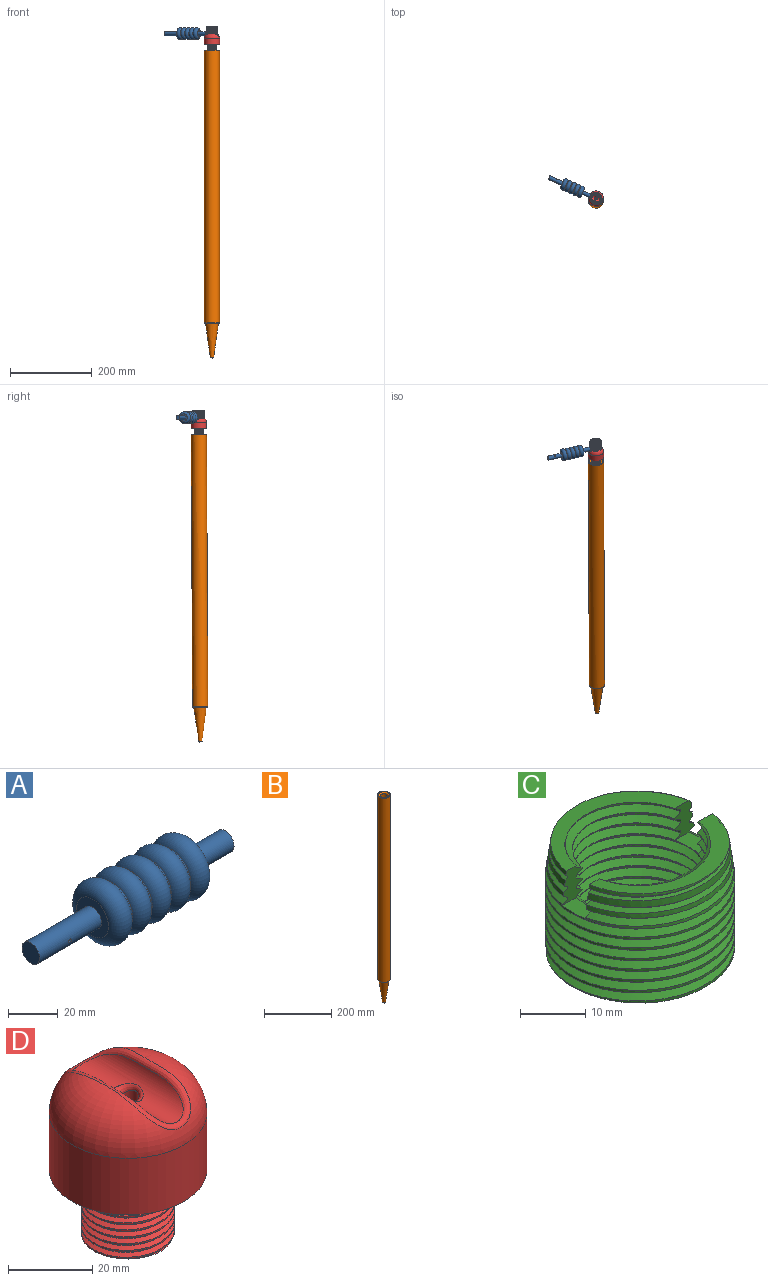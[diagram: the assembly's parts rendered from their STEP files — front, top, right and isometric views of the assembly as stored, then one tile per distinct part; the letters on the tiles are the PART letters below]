
ASSEMBLY  parts=4 mates=3
PART A: 18 faces, bbox 110x31.4x31.4 mm
  f0: cylinder r=5mm len=35mm, axis (-1,0,0), area 1081.4mm2, adj f3,f4,f15,f17
  f1: torus R=11.4mm, axis (-1,0,0), area 80.2mm2, adj f2,f14
  f2: torus R=9mm, axis (-1,0,0), area 1213.5mm2, adj f1,f3
  f3: plane 18x18mm, normal (-1,0,0), area 175.9mm2, adj f0,f2
  f4: plane 10x10mm, normal (-1,0,0), area 78.5mm2, adj f0
  f5: plane 10x10mm, normal (1,0,0), area 78.5mm2, adj f6
  f6: cylinder r=5mm len=20mm, axis (-1,0,0), area 628.3mm2, adj f5,f7
  f7: plane 18x18mm, normal (1,0,0), area 175.9mm2, adj f6,f8
  f8: torus R=9mm, axis (-1,0,0), area 1213.5mm2, adj f7,f9
  f9: torus R=11.4mm, axis (-1,0,0), area 80.2mm2, adj f8,f10
  f10: torus R=9mm, axis (-1,0,0), area 1069.8mm2, adj f9,f11
  f11: torus R=11.4mm, axis (-1,0,0), area 80.2mm2, adj f10,f12
  f12: torus R=9mm, axis (-1,0,0), area 1069.8mm2, adj f11,f13
  f13: torus R=11.4mm, axis (-1,0,0), area 80.2mm2, adj f12,f14
  f14: torus R=9mm, axis (-1,0,0), area 1069.8mm2, adj f1,f13
  f15: cylinder r=2.25mm len=5mm, axis (0,-1,0), area 67mm2, adj f0,f16
  f16: plane 4.5x4.5mm, normal (0,1,0), area 14.1mm2, adj f15,f17
  f17: cylinder r=0.75mm len=5mm, axis (0,1,0), area 23.4mm2, adj f0,f16
PART B: 10 faces, bbox 40.6x40.6x755 mm
  f0: plane 35.5x35.5mm, normal (0,0,-1), area 210.5mm2, adj f1,f9
  f1: cone r=15.75mm half-angle=7.9deg, axis (0,0,1), area 5279mm2, adj f0,f2
  f2: torus R=2.26mm, axis (0,0,1), area 62.4mm2, adj f1,f3
  f3: plane 4.52x4.52mm, normal (0,0,-1), area 16mm2, adj f2
  f4: plane 22x22mm, normal (0,0,1), area 380.1mm2, adj f5
  f5: cylinder r=11mm len=43mm, axis (0,0,1), area 2971.9mm2, adj f4,f6
  f6: torus R=16mm, axis (0,0,1), area 632.5mm2, adj f5,f7
  f7: plane 37.5x37.5mm, normal (0,0,1), area 300.2mm2, adj f6,f8
  f8: cylinder r=18.75mm len=669mm, axis (0,0,1), area 78814.7mm2, adj f7,f9
  f9: torus R=17.75mm, axis (0,0,1), area 181.5mm2, adj f0,f8
PART C: 67 faces, bbox 29.9x34.4x22.6 mm
  f0: bspline ~29.17x16.84mm, area 16.2mm2, adj f2,f3,f8,f29,f66
  f1: bspline ~21.88x16.84mm, area 4mm2, adj f19,f20,f34,f61
  f2: plane 6.02x4.22mm, normal (0,1,0), area 17.3mm2, adj f0,f5,f8,f9,f10,f14,f15,f16
  f3: plane 6.02x4.31mm, normal (0,1,0), area 17.2mm2, adj f0,f8,f9,f10,f14,f15,f16,f22
  f4: plane 6.02x4.31mm, normal (0,-1,0), area 17.1mm2, adj f7,f11,f12,f13,f17,f18,f19,f21
  f5: bspline ~33.69x29.17mm, area 858.4mm2, adj f2,f6,f28,f35,f36,f62
  f6: cylinder r=14.59mm len=29.17mm, axis (0,0,-1), area 442.2mm2, adj f5,f7,f36,f37,f62,f65
  f7: bspline ~33.69x29.17mm, area 882.5mm2, adj f4,f6,f35,f36,f65
  f8: plane 26.86x11.33mm, normal (0,0,1), area 85.6mm2, adj f0,f2,f3,f57,f58,f66
  f9: bspline ~29.17x16.84mm, area 28.7mm2, adj f2,f3,f30,f64
  f10: bspline ~29.17x16.84mm, area 40.6mm2, adj f2,f3,f31,f63
  f11: bspline ~29.17x16.84mm, area 22.9mm2, adj f4,f20,f33,f61
  f12: bspline ~29.17x16.84mm, area 34.6mm2, adj f4,f20,f32,f60
  f13: bspline ~29.17x16.84mm, area 46.6mm2, adj f4,f20,f35,f59
  f14: bspline ~29.17x16.84mm, area 21.3mm2, adj f2,f3,f29,f64
  f15: bspline ~29.17x16.84mm, area 35.1mm2, adj f2,f3,f30,f63
  f16: bspline ~29.17x16.84mm, area 49.3mm2, adj f2,f3,f31,f62
  f17: bspline ~29.17x16.84mm, area 28.2mm2, adj f4,f20,f33,f60
  f18: bspline ~29.17x16.84mm, area 42.2mm2, adj f4,f20,f32,f59
  f19: plane 27.4x11.98mm, normal (0,0,1), area 88.6mm2, adj f1,f4,f20,f27,f34,f49,f50,f61
  f20: plane 6.02x4.21mm, normal (0,-1,0), area 17.2mm2, adj f1,f11,f12,f13,f17,f18,f19,f21
  f21: cylinder r=10.39mm len=20.77mm, axis (0,0,-1), area 71.1mm2, adj f4,f20,f28,f36,f39,f41,f45
  f22: cylinder r=10.39mm len=20.16mm, axis (0,0,-1), area 3.6mm2, adj f2,f3,f40,f54
  f23: cylinder r=10.39mm len=20.16mm, axis (0,0,-1), area 3.6mm2, adj f4,f20,f42,f46
  f24: cylinder r=10.39mm len=20.16mm, axis (0,0,-1), area 3.6mm2, adj f2,f3,f51,f55
  f25: cylinder r=10.39mm len=20.16mm, axis (0,0,-1), area 3.6mm2, adj f4,f20,f43,f48
  f26: cylinder r=10.39mm len=20.16mm, axis (0,0,-1), area 3.6mm2, adj f2,f3,f52,f58
  f27: cylinder r=10.39mm len=1.66mm, axis (0,0,-1), area 0mm2, adj f19,f20,f50
  f28: plane 5.04x3.36mm, normal (0,0,1), area 15.1mm2, adj f2,f5,f20,f21,f35,f41
  f29: cylinder r=13.39mm len=26.3mm, axis (0,0,-1), area 6.1mm2, adj f0,f2,f3,f14
  f30: cylinder r=13.39mm len=26.3mm, axis (0,0,-1), area 6.1mm2, adj f2,f3,f9,f15
  f31: cylinder r=13.39mm len=26.3mm, axis (0,0,-1), area 6.1mm2, adj f2,f3,f10,f16
  f32: cylinder r=13.39mm len=26.3mm, axis (0,0,-1), area 6.1mm2, adj f4,f12,f18,f20
  f33: cylinder r=13.39mm len=26.3mm, axis (0,0,-1), area 6.1mm2, adj f4,f11,f17,f20
  f34: cylinder r=13.39mm len=4.11mm, axis (0,0,-1), area 0.2mm2, adj f1,f19,f20
  f35: cylinder r=13.39mm len=26.77mm, axis (0,0,-1), area 20.3mm2, adj f4,f5,f7,f13,f20,f28,f36
  f36: plane 29.01x28.75mm, normal (0,0,-1), area 235mm2, adj f5,f6,f7,f21,f35,f38,f39,f41
  f37: plane 5x3.24mm, normal (0,0,1), area 14.9mm2, adj f3,f4,f6,f38
  f38: cylinder r=11.62mm len=23.23mm, axis (0,0,1), area 329.8mm2, adj f2,f3,f4,f36,f37,f39,f40,f41
  f39: bspline ~26.83x23.23mm, area 707.9mm2, adj f4,f21,f36,f38
  f40: bspline ~23.23x13.41mm, area 41.9mm2, adj f2,f3,f22,f38
  f41: bspline ~26.83x23.23mm, area 701.3mm2, adj f2,f21,f28,f36,f38
  f42: bspline ~23.23x13.41mm, area 41.9mm2, adj f4,f20,f23,f44
  f43: bspline ~23.23x13.41mm, area 41.9mm2, adj f4,f20,f25,f44
  f44: cylinder r=11.62mm len=22.69mm, axis (0,0,1), area 14.2mm2, adj f4,f20,f42,f43
  f45: bspline ~23.23x13.41mm, area 41.9mm2, adj f4,f20,f21,f47
  f46: bspline ~23.23x13.41mm, area 41.9mm2, adj f4,f20,f23,f47
  f47: cylinder r=11.62mm len=22.69mm, axis (0,0,1), area 14.2mm2, adj f4,f20,f45,f46
  f48: bspline ~23.23x13.41mm, area 41.9mm2, adj f4,f20,f25,f49
  f49: cylinder r=11.62mm len=22.69mm, axis (0,0,1), area 14mm2, adj f4,f19,f20,f48,f50
  f50: bspline ~23.23x13.41mm, area 20.6mm2, adj f19,f20,f27,f49
  f51: bspline ~23.23x13.41mm, area 41.9mm2, adj f2,f3,f24,f53
  f52: bspline ~23.23x13.41mm, area 41.9mm2, adj f2,f3,f26,f53
  f53: cylinder r=11.62mm len=22.69mm, axis (0,0,1), area 14.2mm2, adj f2,f3,f51,f52
  f54: bspline ~23.23x13.41mm, area 41.9mm2, adj f2,f3,f22,f56
  f55: bspline ~23.23x13.41mm, area 41.9mm2, adj f2,f3,f24,f56
  f56: cylinder r=11.62mm len=22.69mm, axis (0,0,1), area 14.2mm2, adj f2,f3,f54,f55
  f57: cylinder r=11.62mm len=6.62mm, axis (0,0,1), area 0.9mm2, adj f3,f8,f58
  f58: bspline ~23.23x13.41mm, area 27.6mm2, adj f2,f3,f8,f26,f57
  f59: cone r=13.74mm half-angle=8deg, axis (0,0,-1), area 27.8mm2, adj f4,f13,f18,f20
  f60: cone r=13.74mm half-angle=8deg, axis (0,0,-1), area 40.2mm2, adj f4,f12,f17,f20
  f61: cone r=13.74mm half-angle=8deg, axis (0,0,-1), area 44.1mm2, adj f1,f4,f11,f19,f20
  f62: cone r=13.74mm half-angle=8deg, axis (0,0,-1), area 19.9mm2, adj f2,f3,f5,f6,f16
  f63: cone r=13.74mm half-angle=8deg, axis (0,0,-1), area 34.1mm2, adj f2,f3,f10,f15
  f64: cone r=13.74mm half-angle=8deg, axis (0,0,-1), area 46.1mm2, adj f2,f3,f9,f14
  f65: cone r=13.74mm half-angle=8deg, axis (0,0,-1), area 0.2mm2, adj f4,f6,f7
  f66: cone r=13.74mm half-angle=8deg, axis (0,0,-1), area 11.1mm2, adj f0,f3,f8
PART D: 17 faces, bbox 38.2x38.2x48.6 mm
  f0: cylinder r=11.1mm len=22.2mm, axis (0,0,-1), area 322.6mm2, adj f1,f2,f5,f9
  f1: bspline ~25.63x22.2mm, area 798.7mm2, adj f0,f3,f5,f9
  f2: bspline ~25.63x22.2mm, area 799.3mm2, adj f0,f3,f5,f9
  f3: cylinder r=10mm len=20mm, axis (0,0,1), area 192.3mm2, adj f1,f2,f5,f9
  f4: cylinder r=18.75mm len=37.5mm, axis (0,0,-1), area 1943.9mm2, adj f5,f6
  f5: plane 38.17x38.17mm, normal (0,0,-1), area 753mm2, adj f0,f1,f2,f3,f4
  f6: torus R=7.25mm, axis (0,0,1), area 1272mm2, adj f4,f13
  f7: cylinder r=6mm len=32.83mm, axis (0,-1,0), area 407mm2, adj f13,f14
  f8: cylinder r=6.5mm len=18.85mm, axis (0,0,1), area 769.8mm2, adj f9,f16
  f9: plane 21.87x21.79mm, normal (0,0,-1), area 218.8mm2, adj f0,f1,f2,f3,f8
  f10: sphere r=7mm, area 285.3mm2, adj f11,f15
  f11: cone r=6.5mm half-angle=3.5deg, axis (0,0,1), area 333.4mm2, adj f10,f16
  f12: cylinder r=2.5mm len=5.44mm, axis (0,0,1), area 76.1mm2, adj f14,f15
  f13: bspline ~35.54x15.12mm, area 183.5mm2, adj f6,f7
  f14: bspline ~8.01x6.4mm, area 35.7mm2, adj f7,f12
  f15: torus R=4.5mm, axis (0,0,-1), area 37.5mm2, adj f10,f12
  f16: torus R=11.5mm, axis (0,0,1), area 12.4mm2, adj f8,f11
PLACE A rot(axis=(-0.93,0.2,-0.32),67.4deg) t=(-246.92,-37.31,575.43)mm
PLACE B rot(axis=(0,0,1),180deg) t=(-232.69,-47.56,-220.69)mm fixed
PLACE C rot(axis=(0.75,0.66,0),179.8deg) t=(-232.69,-43.55,593.9)mm
PLACE D rot(axis=(0,0,1),66deg) t=(-232.69,-43.77,547.46)mm
MATE cylindrical B.f1 <-> C.f6  axis (0,0,1) through (-232.69,-43.97,507.8)mm
MATE cylindrical D.f8 <-> B.f1  axis (0,0,1) through (-232.69,-43.82,537.89)mm
MATE cylindrical A.f0 <-> D.f7  axis (-0.91,0.41,0) through (-331.44,0.27,575.25)mm
